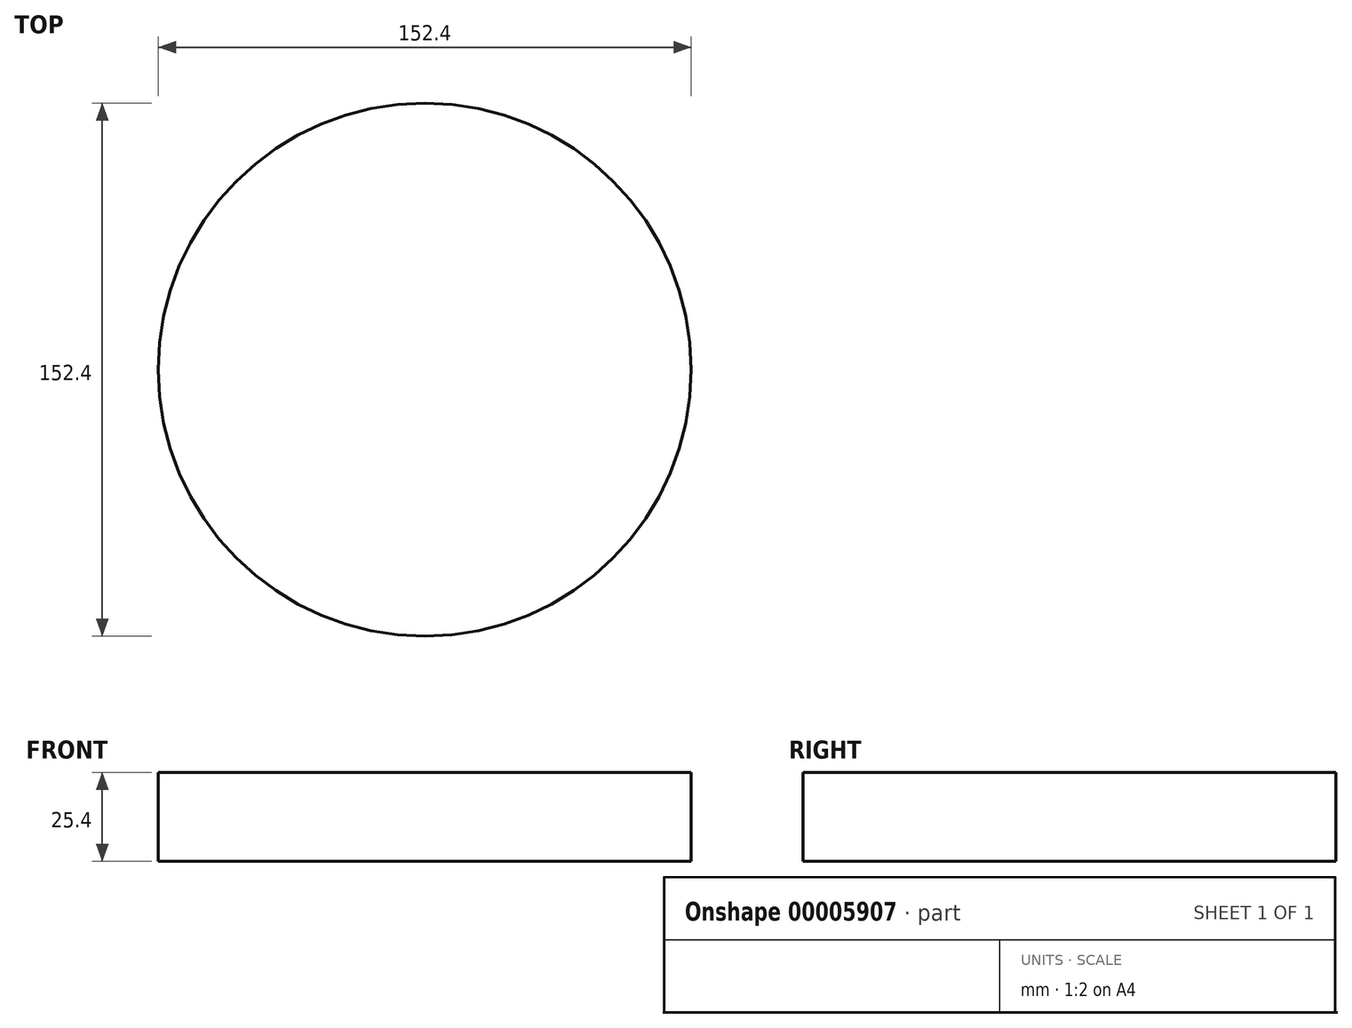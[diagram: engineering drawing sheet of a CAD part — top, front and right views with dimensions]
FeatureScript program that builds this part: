
annotation { "Feature Type Name" : "Feature", "Feature Type Description" : "" }
export const myFeature = defineFeature(function(context is Context, id is Id, definition is map)
    precondition{}
    {
        {
            var Q0;
            Q0=qCreatedBy(makeId("Top.planeOp"),FACE);
            var sketch = newSketch(context, id + "F0", { "sketchPlane" : qUnion([Q0])});
            skCircle(sketch, "E0", {"center": v(0, 0) * mm, "radius": 76.2 * mm});
            skSolve(sketch);
        }
        {
            var Q0;
            Q0=makeQuery(id+"F0.imprint","IMPRINT",FACE,{"disambiguationData":[TD([[makeQuery(id+"F0.imprint","IMPRINT",EDGE,{"derivedFrom":sQuery(id+"F0.wireOp",EDGE,"E0")}),1.0]])]});
            extrude(context, id + "F1", {"entities" : qUnion([Q0]), "depth" : 25.4 * mm});
        }
    });
